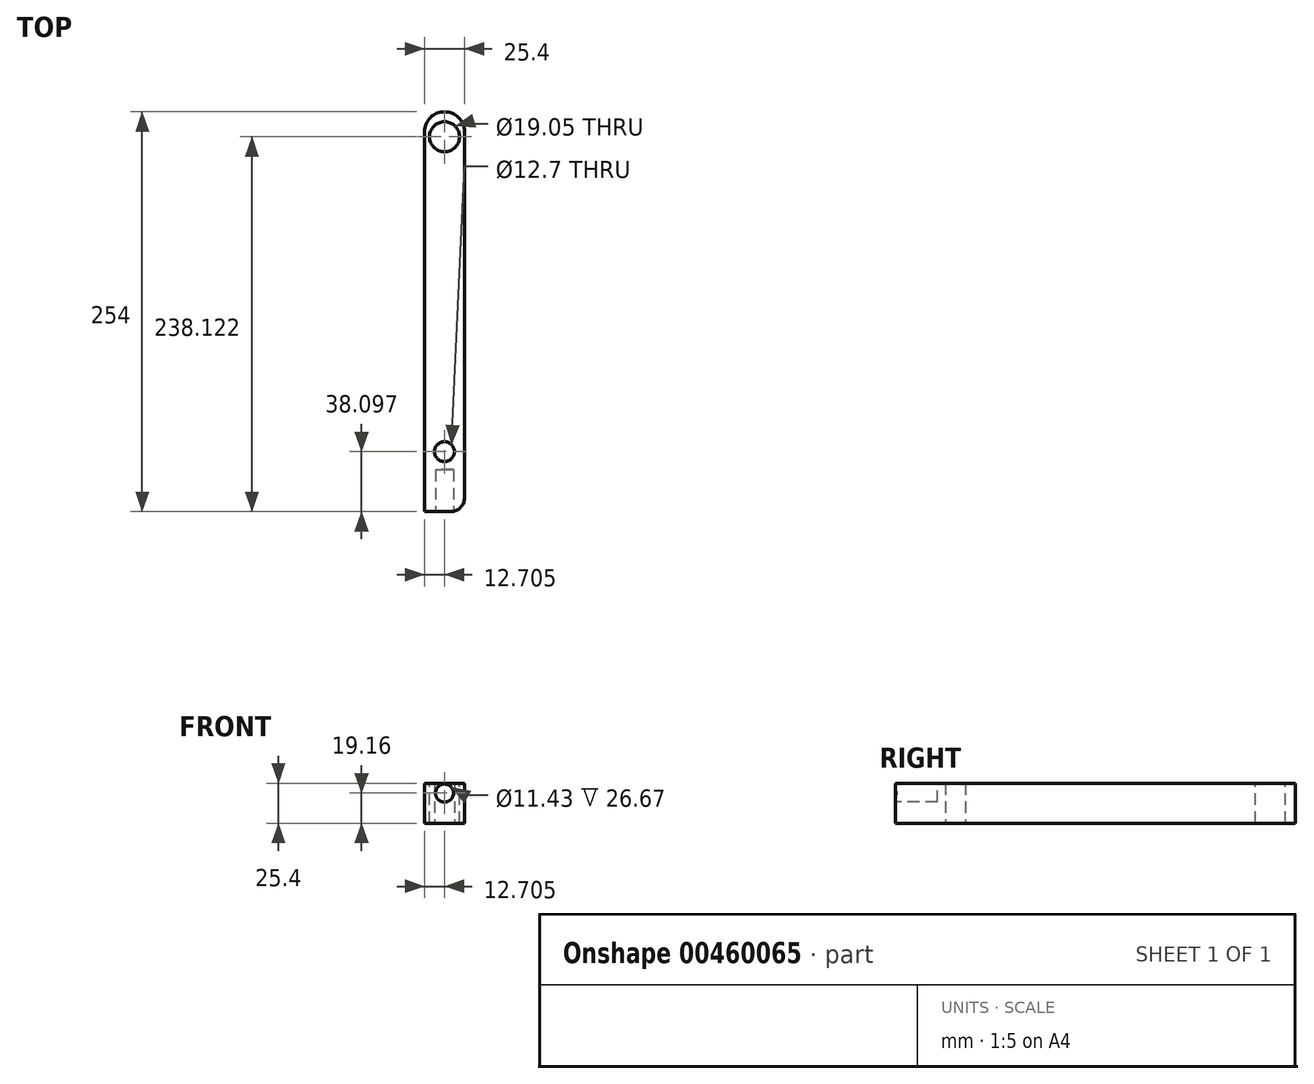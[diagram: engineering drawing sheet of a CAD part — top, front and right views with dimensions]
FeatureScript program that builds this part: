
annotation { "Feature Type Name" : "Feature", "Feature Type Description" : "" }
export const myFeature = defineFeature(function(context is Context, id is Id, definition is map)
    precondition{}
    {
        {
            var Q0;
            Q0=qCreatedBy(makeId("Top.planeOp"),FACE);
            var sketch = newSketch(context, id + "F0", { "sketchPlane" : qUnion([Q0])});
            skLineSegment(sketch, "E0.top", {"start": v(-45.9, 140.46) * mm, "end": v(-20.5, 140.46) * mm});
            skLineSegment(sketch, "E1", {"start": v(-20.5, 140.46) * mm, "end": v(-20.5, -113.54) * mm});
            skLineSegment(sketch, "E2", {"start": v(-20.5, -113.54) * mm, "end": v(-45.9, -113.54) * mm});
            skLineSegment(sketch, "E3", {"start": v(-45.9, -113.54) * mm, "end": v(-45.9, 140.46) * mm});
            skPoint(sketch, "E4.center.orphan", {"position": v(-20.5, -126.24) * mm});
            skCircle(sketch, "E5", {"center": v(-33.2, 124.58) * mm, "radius": 9.53 * mm});
            skPoint(sketch, "E5.centerSnap0", {"position": v(-33.2, 140.46) * mm});
            skPoint(sketch, "E6.trimOffspring.end.orphan", {"position": v(-20.5, -138.94) * mm});
            skSolve(sketch);
        }
        {
            var Q0;
            Q0=makeQuery(id+"F0.imprint","IMPRINT",FACE,{"disambiguationData":[TD([[makeQuery(id+"F0.imprint","IMPRINT",EDGE,{"derivedFrom":sQuery(id+"F0.wireOp",EDGE,"E0.top")}),-1.0]])]});
            var Q1;
            Q1=makeQuery(id+"F0.imprint","IMPRINT",FACE,{"disambiguationData":[TD([[makeQuery(id+"F0.imprint","IMPRINT",EDGE,{"derivedFrom":sQuery(id+"F0.wireOp",EDGE,"E2")}),1.0]])]});
            extrude(context, id + "F1", {"entities" : qUnion([Q0, Q1]), "oppositeDirection" : true, "depth" : 25.4 * mm});
        }
        {
            var Q0;
            Q0=makeQuery(id+"F1.opExtrude","SWEPT_EDGE",EDGE,{"disambiguationData":[OSD([sQuery(id+"F0.wireOp",EDGE,"E0.top"),sQuery(id+"F0.wireOp",EDGE,"E3")])]});
            var Q1;
            Q1=makeQuery(id+"F1.opExtrude","SWEPT_EDGE",EDGE,{"disambiguationData":[OSD([sQuery(id+"F0.wireOp",EDGE,"E0.top"),sQuery(id+"F0.wireOp",EDGE,"E1")])]});
            fillet(context, id + "F2", {"entities" : qUnion([Q0, Q1]), "radius" : 12.7 * mm, "tangentPropagation" : true, "allowEdgeOverflow" : false});
        }
        {
            var Q0;
            Q0=makeQuery(id+"F1.opExtrude","SWEPT_FACE",FACE,{"disambiguationData":[OSD([sQuery(id+"F0.wireOp",EDGE,"E2")])]});
            var sketch = newSketch(context, id + "F3", { "sketchPlane" : qUnion([Q0])});
            skCircle(sketch, "E7", {"center": v(-33.2, -6.24) * mm, "radius": 5.72 * mm});
            skPoint(sketch, "E7.centerSnap0", {"position": v(-33.2, 0) * mm});
            skSolve(sketch);
        }
        {
            var Q0;
            Q0=makeQuery(id+"F3.imprint","IMPRINT",FACE,{"disambiguationData":[TD([[makeQuery(id+"F3.imprint","IMPRINT",EDGE,{"derivedFrom":sQuery(id+"F3.wireOp",EDGE,"E7")}),1.0]])]});
            extrude(context, id + "F4", {"entities" : qUnion([Q0]), "operationType" : NewBodyOperationType.REMOVE, "oppositeDirection" : true, "depth" : 26.67 * mm});
        }
        {
            var Q0;
            Q0=makeQuery(id+"F1.opExtrude","CAP_FACE",FACE,{"disambiguationData":[OSD([sQuery(id+"F0.wireOp",EDGE,"E0.top"),sQuery(id+"F0.wireOp",EDGE,"E1"),sQuery(id+"F0.wireOp",EDGE,"E2"),sQuery(id+"F0.wireOp",EDGE,"E3"),sQuery(id+"F0.wireOp",EDGE,"E5")])],"isStart":false});
            var sketch = newSketch(context, id + "F5", { "sketchPlane" : qUnion([Q0])});
            skLineSegment(sketch, "E8", {"start": v(-33.2, 113.54) * mm, "end": v(-33.2, 75.44) * mm});
            skCircle(sketch, "E9", {"center": v(-33.2, 75.44) * mm, "radius": 6.35 * mm});
            skSolve(sketch);
        }
        {
            var Q0;
            Q0=qSketchRegion(id+"F5",true);
            extrude(context, id + "F6", {"entities" : qUnion([Q0]), "operationType" : NewBodyOperationType.REMOVE, "oppositeDirection" : true, "depth" : 25.4 * mm});
        }
        {
            var Q0;
            Q0=makeQuery(id+"F1.opExtrude","SWEPT_EDGE",EDGE,{"disambiguationData":[OSD([sQuery(id+"F0.wireOp",EDGE,"E1"),sQuery(id+"F0.wireOp",EDGE,"E2")])]});
            fillet(context, id + "F7", {"entities" : qUnion([Q0]), "radius" : 8.9 * mm, "tangentPropagation" : true, "allowEdgeOverflow" : false});
        }
    });
